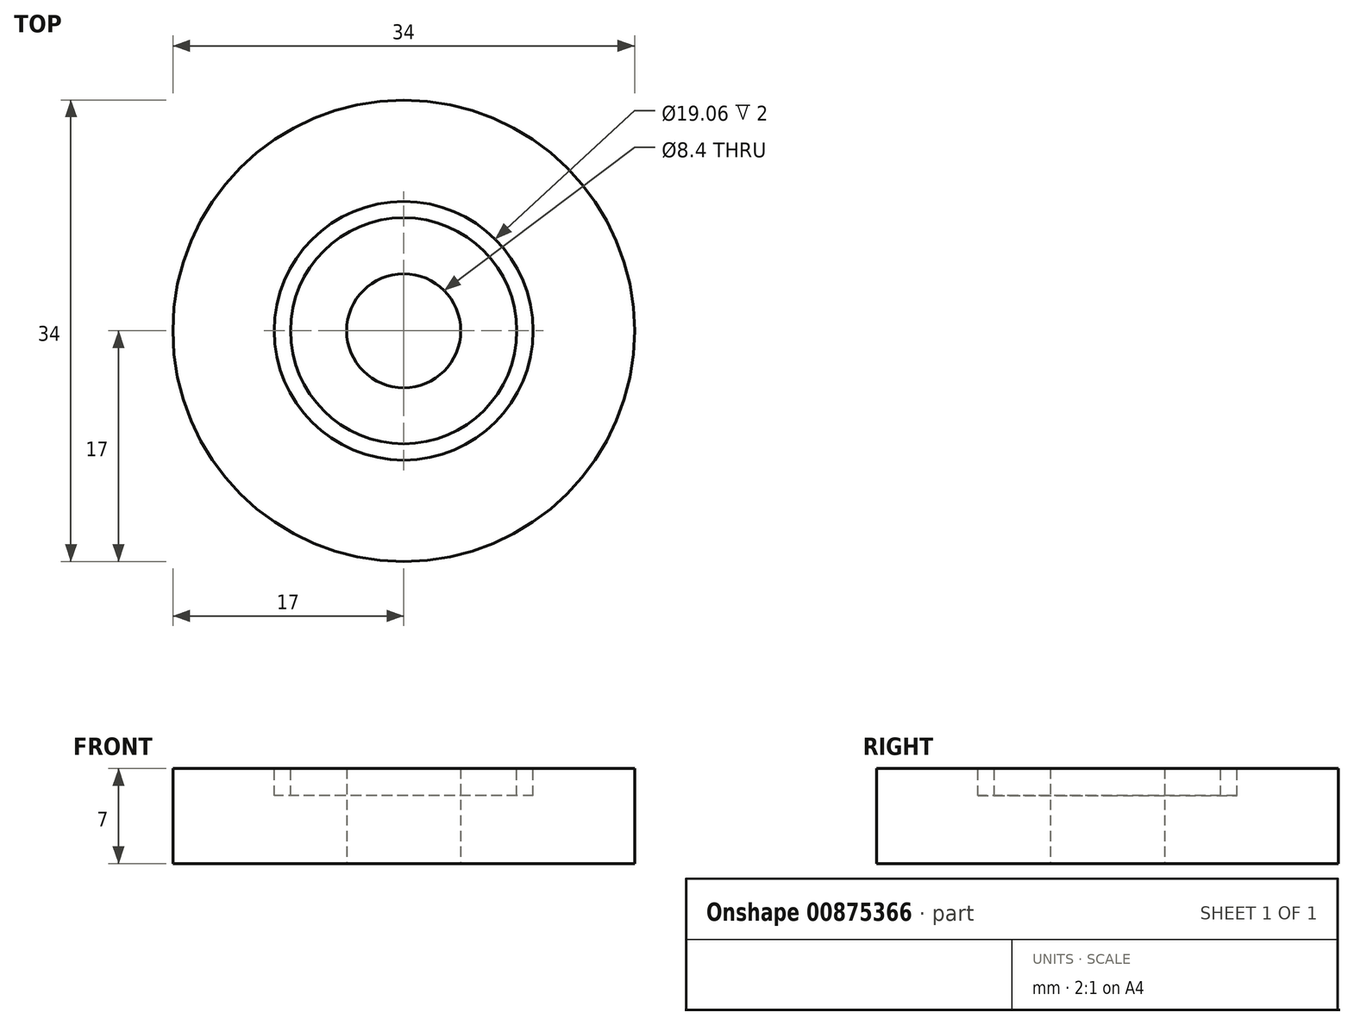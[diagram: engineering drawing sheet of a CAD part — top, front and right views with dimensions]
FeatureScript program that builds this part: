
annotation { "Feature Type Name" : "Feature", "Feature Type Description" : "" }
export const myFeature = defineFeature(function(context is Context, id is Id, definition is map)
    precondition{}
    {
        {
            var Q0;
            Q0=qCreatedBy(makeId("Front.planeOp"),FACE);
            var sketch = newSketch(context, id + "F0", { "sketchPlane" : qUnion([Q0])});
            skLineSegment(sketch, "E0", {"start": v(0, 0) * mm, "end": v(17, 0) * mm});
            skLineSegment(sketch, "E1", {"start": v(17, 0) * mm, "end": v(17, 7) * mm});
            skLineSegment(sketch, "E2", {"start": v(8.33, 7) * mm, "end": v(8.33, 5) * mm});
            skLineSegment(sketch, "E3", {"start": v(8.33, 5) * mm, "end": v(9.53, 5) * mm});
            skLineSegment(sketch, "E4", {"start": v(9.53, 5) * mm, "end": v(9.53, 7) * mm});
            skLineSegment(sketch, "E5", {"start": v(9.53, 7) * mm, "end": v(17, 7) * mm});
            skLineSegment(sketch, "E6", {"start": v(0, 7) * mm, "end": v(0, 0) * mm});
            skLineSegment(sketch, "E7", {"start": v(8.33, 7) * mm, "end": v(0, 7) * mm});
            skLineSegment(sketch, "E8", {"start": v(0, 14.41) * mm, "end": v(0, -4.52) * mm, "construction": true});
            skSolve(sketch);
        }
        {
            var Q0;
            {var subQ0=sQuery(id+"F0.wireOp",EDGE,"E1");Q0=makeQuery(id+"F0.imprint","IMPRINT",FACE,{"disambiguationData":[TD([[makeQuery(id+"F0.imprint","IMPRINT",EDGE,{"derivedFrom":subQ0}),1.0]])]});}
            var Q1;
            Q1=sQuery(id+"F0.wireOp",EDGE,"E8");
            revolve(context, id + "F1", {"surfaceOperationType" : NewSurfaceOperationType.NEW, "entities" : qUnion([Q0]), "axis" : qUnion([Q1]), "revolveType" : RevolveType.FULL});
        }
        {
            var Q0;
            Q0=makeQuery(id+"F1.opRevolve","SWEPT_FACE",FACE,{"disambiguationData":[OSD([sQuery(id+"F0.wireOp",EDGE,"E7")])]});
            var sketch = newSketch(context, id + "F2", { "sketchPlane" : qUnion([Q0])});
            skPoint(sketch, "E9", {"position": v(0, 0) * mm});
            skSolve(sketch);
        }
        {
            var Q0;
            Q0=sQuery(id+"F2.wireOp",VERTEX,"E9");
            var Q1;
            Q1=makeQuery(id+"F1.opRevolve","SWEPT_BODY",BODY,{"disambiguationData":[OSD([sQuery(id+"F0.wireOp",EDGE,"E0"),sQuery(id+"F0.wireOp",EDGE,"E1"),sQuery(id+"F0.wireOp",EDGE,"E2"),sQuery(id+"F0.wireOp",EDGE,"E3"),sQuery(id+"F0.wireOp",EDGE,"E4"),sQuery(id+"F0.wireOp",EDGE,"E5"),sQuery(id+"F0.wireOp",EDGE,"E6"),sQuery(id+"F0.wireOp",EDGE,"E7")])]});
            hole(context, id + "F3", {"style" : HoleStyle.SIMPLE, "endStyle" : HoleEndStyle.THROUGH, "standardTappedOrClearance" : lookupTablePath({ "fit" : "Close", "standard" : "ISO", "size" : "M8", "type" : "Clearance" }), "standardBlindInLast" : lookupTablePath({ "fit" : "Close", "standard" : "ISO", "engagement" : "75%", "pitch" : "1.25 mm", "size" : "M8", "type" : "Clearance & tapped" }), "holeDiameter" : 8.4 * mm, "majorDiameter" : 5 * mm, "isTappedThrough" : true, "tappedDepth" : 12 * mm, "tapClearance" : 3, "locations" : qUnion([Q0]), "scope" : qUnion([Q1]), "startStyle" : HoleStartStyle.SKETCH});
        }
    });
